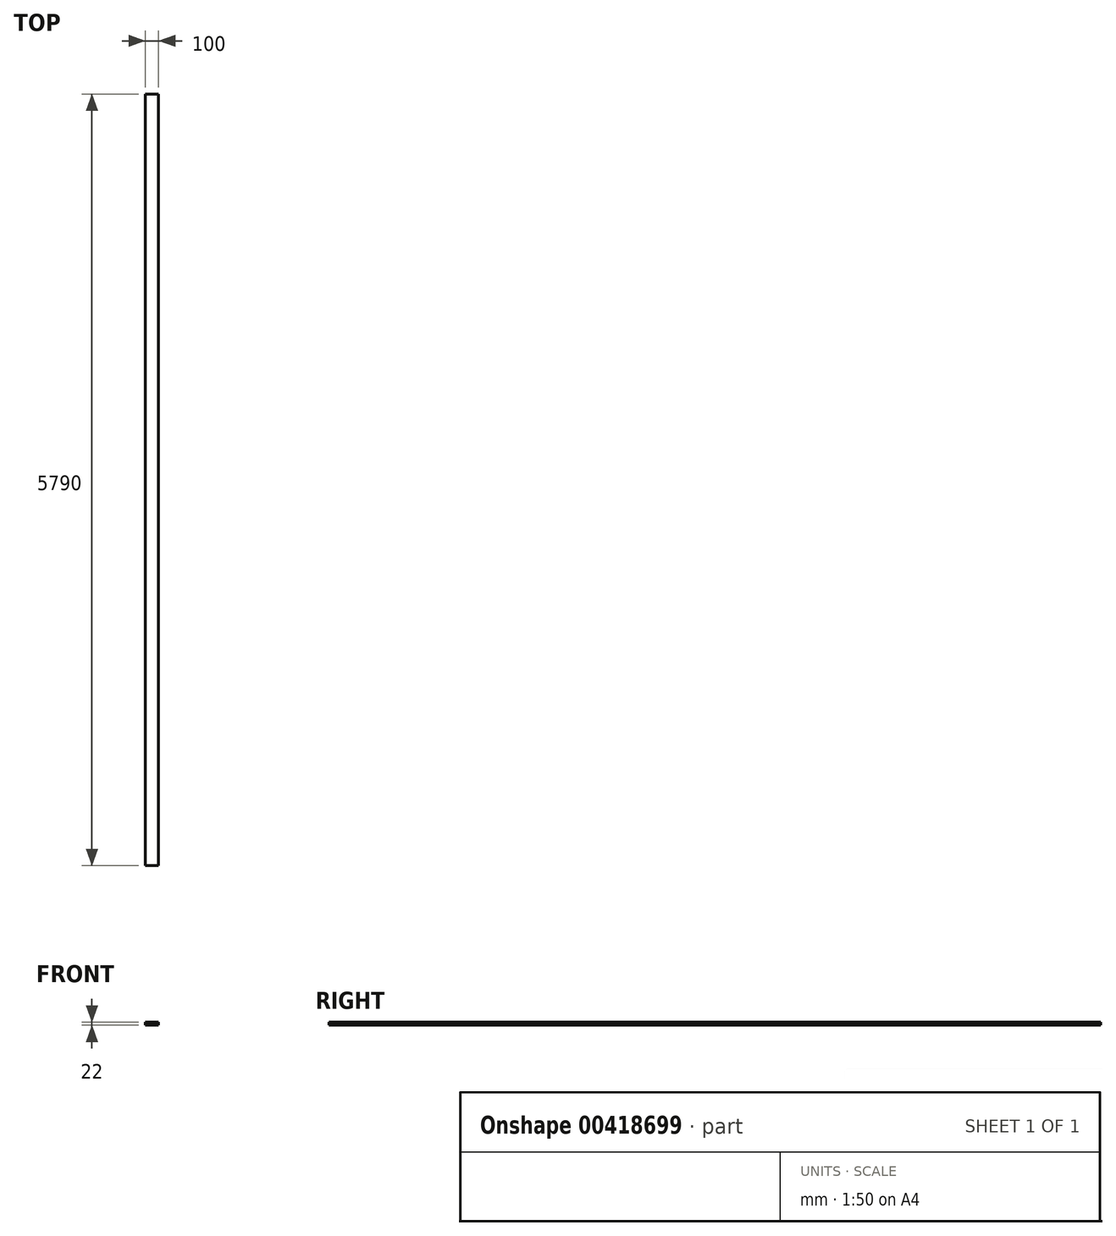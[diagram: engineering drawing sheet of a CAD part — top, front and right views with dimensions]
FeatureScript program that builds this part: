
annotation { "Feature Type Name" : "Feature", "Feature Type Description" : "" }
export const myFeature = defineFeature(function(context is Context, id is Id, definition is map)
    precondition{}
    {
        {
            var Q0;
            Q0=qCreatedBy(makeId("Front.planeOp"),FACE);
            var sketch = newSketch(context, id + "F0", { "sketchPlane" : qUnion([Q0])});
            skLineSegment(sketch, "E0.bottom", {"start": v(50, 11) * mm, "end": v(-50, 11) * mm});
            skLineSegment(sketch, "E0.top", {"start": v(50, -11) * mm, "end": v(-50, -11) * mm});
            skLineSegment(sketch, "E0.left", {"start": v(50, 11) * mm, "end": v(50, -11) * mm});
            skLineSegment(sketch, "E0.right", {"start": v(-50, 11) * mm, "end": v(-50, -11) * mm});
            skPoint(sketch, "E0.middle", {"position": v(0, 0) * mm});
            skSolve(sketch);
        }
        {
            var Q0;
            Q0 = qSketchRegion(id + "F0", true);
            extrude(context, id + "F1", {"entities" : qUnion([Q0]), "endBound" : BoundingType.SYMMETRIC, "depth" : (5000 + 375 + 375 + 40) * mm});
        }
    });
